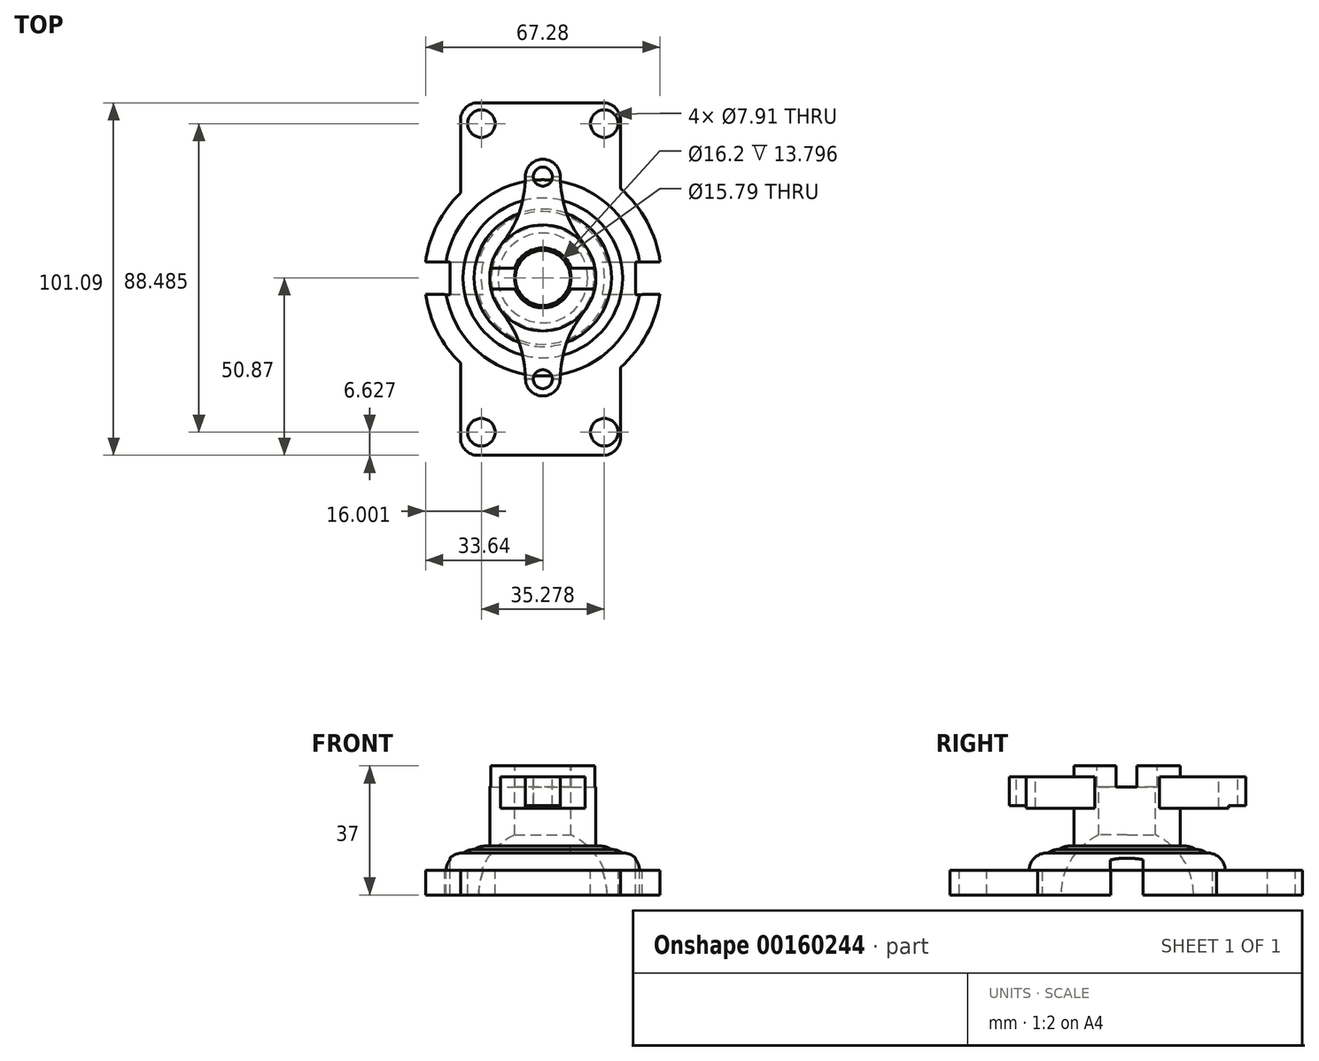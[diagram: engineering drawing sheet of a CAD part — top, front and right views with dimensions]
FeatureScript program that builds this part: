
annotation { "Feature Type Name" : "Feature", "Feature Type Description" : "" }
export const myFeature = defineFeature(function(context is Context, id is Id, definition is map)
    precondition{}
    {
        {
            var Q0;
            Q0=qCreatedBy(makeId("Top.planeOp"),FACE);
            var sketch = newSketch(context, id + "F0", { "sketchPlane" : qUnion([Q0])});
            skLineSegment(sketch, "E0.bottom", {"start": v(-23.62, 50.22) * mm, "end": v(22.27, 50.22) * mm});
            skLineSegment(sketch, "E0.top", {"start": v(-23.62, -50.87) * mm, "end": v(22.27, -50.87) * mm});
            skLineSegment(sketch, "E0.left", {"start": v(-23.62, 50.22) * mm, "end": v(-23.62, -50.87) * mm});
            skLineSegment(sketch, "E0.right", {"start": v(22.27, 50.22) * mm, "end": v(22.27, -50.87) * mm});
            skCircle(sketch, "E1", {"center": v(0, 0) * mm, "radius": 33.95 * mm});
            skSolve(sketch);
        }
        {
            var Q0;
            Q0 = qSketchRegion(id + "F0", true);
            extrude(context, id + "F1", {"entities" : qUnion([Q0]), "depth" : 7 * mm});
        }
        {
            var Q0;
            Q0=qCreatedBy(makeId("Top.planeOp"),FACE);
            var sketch = newSketch(context, id + "F2", { "sketchPlane" : qUnion([Q0])});
            skLineSegment(sketch, "E2.bottom", {"start": v(-35.85, -4.72) * mm, "end": v(38.25, -4.72) * mm});
            skLineSegment(sketch, "E2.top", {"start": v(-35.85, 4.53) * mm, "end": v(38.25, 4.53) * mm});
            skLineSegment(sketch, "E2.left", {"start": v(-35.85, -4.72) * mm, "end": v(-35.85, 4.53) * mm});
            skLineSegment(sketch, "E2.right", {"start": v(38.25, -4.72) * mm, "end": v(38.25, 4.53) * mm});
            skCircle(sketch, "E3", {"center": v(0, 0) * mm, "radius": 17.03 * mm});
            skSolve(sketch);
        }
        {
            var Q0;
            Q0 = qSketchRegion(id + "F2", true);
            extrude(context, id + "F3", {"entities" : qUnion([Q0]), "operationType" : NewBodyOperationType.REMOVE, "depth" : 7 * mm});
        }
        {
            var Q0;
            Q0=makeQuery(id+"F1.opExtrude","CAP_FACE",FACE,{"disambiguationData":[OSD([sQuery(id+"F0.wireOp",EDGE,"E0.bottom"),sQuery(id+"F0.wireOp",EDGE,"E0.top"),sQuery(id+"F0.wireOp",EDGE,"E0.left"),sQuery(id+"F0.wireOp",EDGE,"E0.right"),sQuery(id+"F0.wireOp",EDGE,"E1")])],"isStart":false});
            var sketch = newSketch(context, id + "F4", { "sketchPlane" : qUnion([Q0])});
            skCircle(sketch, "E4", {"center": v(0, 0) * mm, "radius": 28.12 * mm});
            skSolve(sketch);
        }
        {
            var Q0;
            Q0 = qSketchRegion(id + "F4", true);
            extrude(context, id + "F5", {"entities" : qUnion([Q0]), "operationType" : NewBodyOperationType.ADD, "depth" : 5 * mm});
        }
        {
            var Q0;
            Q0=makeQuery(id+"F5.opExtrude","CAP_EDGE",EDGE,{"disambiguationData":[OSD([sQuery(id+"F4.wireOp",EDGE,"E4")])],"isStart":false});
            fillet(context, id + "F6", {"entities" : qUnion([Q0]), "radius" : 5 * mm, "tangentPropagation" : true, "allowEdgeOverflow" : false});
        }
        {
            var Q0;
            Q0=makeQuery(id+"F5.opExtrude","CAP_FACE",FACE,{"disambiguationData":[OSD([sQuery(id+"F4.wireOp",EDGE,"E4")])],"isStart":false});
            var sketch = newSketch(context, id + "F7", { "sketchPlane" : qUnion([Q0])});
            skCircle(sketch, "E5", {"center": v(0, 0) * mm, "radius": 15.22 * mm});
            skSolve(sketch);
        }
        {
            var Q0;
            Q0=makeQuery(id+"F7.imprint","IMPRINT",FACE,{"disambiguationData":[TD([[makeQuery(id+"F7.imprint","IMPRINT",EDGE,{"derivedFrom":sQuery(id+"F7.wireOp",EDGE,"E5")}),1.0]])]});
            extrude(context, id + "F8", {"entities" : qUnion([Q0]), "operationType" : NewBodyOperationType.ADD, "depth" : 25 * mm});
        }
        {
            var Q0;
            Q0=makeQuery(id+"F8.opExtrude","CAP_FACE",FACE,{"disambiguationData":[OSD([sQuery(id+"F7.wireOp",EDGE,"E5")])],"isStart":false});
            var sketch = newSketch(context, id + "F9", { "sketchPlane" : qUnion([Q0])});
            skLineSegment(sketch, "E6.bottom", {"start": v(-18.99, 2.8) * mm, "end": v(19.76, 2.8) * mm});
            skLineSegment(sketch, "E6.top", {"start": v(-18.99, -3.18) * mm, "end": v(19.76, -3.18) * mm});
            skLineSegment(sketch, "E6.left", {"start": v(-18.99, 2.8) * mm, "end": v(-18.99, -3.18) * mm});
            skLineSegment(sketch, "E6.right", {"start": v(19.76, 2.8) * mm, "end": v(19.76, -3.18) * mm});
            skCircle(sketch, "E7", {"center": v(0, 0) * mm, "radius": 8.6 * mm});
            skSolve(sketch);
        }
        {
            var Q0;
            Q0 = qSketchRegion(id + "F9", true);
            extrude(context, id + "F10", {"entities" : qUnion([Q0]), "operationType" : NewBodyOperationType.REMOVE, "oppositeDirection" : true, "depth" : 6 * mm});
        }
        {
            var Q0;
            Q0=makeQuery(id+"F10.boolean.opBoolean","COPY",FACE,{"derivedFrom":makeQuery(id+"F10.opExtrude","CAP_FACE",FACE,{"disambiguationData":[OSD([sQuery(id+"F9.wireOp",EDGE,"E6.bottom"),sQuery(id+"F9.wireOp",EDGE,"E6.top"),sQuery(id+"F9.wireOp",EDGE,"E6.left"),sQuery(id+"F9.wireOp",EDGE,"E6.right"),sQuery(id+"F9.wireOp",EDGE,"E7")])],"isStart":false})});
            var sketch = newSketch(context, id + "F11", { "sketchPlane" : qUnion([Q0])});
            skCircle(sketch, "E8", {"center": v(0, 0) * mm, "radius": 8.1 * mm});
            skSolve(sketch);
        }
        {
            var Q0;
            Q0 = qSketchRegion(id + "F11", true);
            extrude(context, id + "F12", {"entities" : qUnion([Q0]), "operationType" : NewBodyOperationType.REMOVE, "oppositeDirection" : true, "depth" : 30 * mm});
        }
        {
            var Q0;
            {var subQ0=sQuery(id+"F0.wireOp",EDGE,"E1");var subQ1=sQuery(id+"F0.wireOp",EDGE,"E0.left");var subQ6=sQuery(id+"F0.wireOp",EDGE,"E0.right");var subQ7=sQuery(id+"F0.wireOp",EDGE,"E0.bottom");Q0=makeQuery(id+"F3.boolean.opBoolean","SPLIT",FACE,{"disambiguationData":[TD([makeQuery(id+"F1.opExtrude","SWEPT_FACE",FACE,{"disambiguationData":[OSD([subQ7])]})])],"derivedFrom":makeQuery(id+"F1.opExtrude","CAP_FACE",FACE,{"disambiguationData":[OSD([subQ7,sQuery(id+"F0.wireOp",EDGE,"E0.top"),subQ1,subQ6,subQ0])],"isStart":false})});}
            var sketch = newSketch(context, id + "F13", { "sketchPlane" : qUnion([Q0])});
            skCircle(sketch, "E9", {"center": v(-17.64, 44.24) * mm, "radius": 3.96 * mm});
            skCircle(sketch, "E10.MirrorC", {"center": v(17.64, 44.24) * mm, "radius": 3.96 * mm});
            skCircle(sketch, "E11.MirrorC", {"center": v(-17.64, -44.24) * mm, "radius": 3.96 * mm});
            skCircle(sketch, "E12.MirrorC", {"center": v(17.64, -44.24) * mm, "radius": 3.96 * mm});
            skSolve(sketch);
        }
        {
            var Q0;
            Q0=qCreatedBy(makeId("Right.planeOp"),FACE);
            var sketch = newSketch(context, id + "F14", { "sketchPlane" : qUnion([Q0])});
            skLineSegment(sketch, "E13.bottom", {"start": v(-13.4, 33.83) * mm, "end": v(-33.83, 33.83) * mm});
            skLineSegment(sketch, "E13.top", {"start": v(-13.4, 25.54) * mm, "end": v(-33.83, 25.54) * mm});
            skLineSegment(sketch, "E13.left", {"start": v(-13.4, 33.83) * mm, "end": v(-13.4, 25.54) * mm});
            skLineSegment(sketch, "E13.right", {"start": v(-33.83, 33.83) * mm, "end": v(-33.83, 25.54) * mm});
            skLineSegment(sketch, "E14.bottom", {"start": v(13.75, 33.83) * mm, "end": v(34.03, 33.83) * mm});
            skLineSegment(sketch, "E14.top", {"start": v(13.75, 25.54) * mm, "end": v(34.03, 25.54) * mm});
            skLineSegment(sketch, "E14.left", {"start": v(13.75, 33.83) * mm, "end": v(13.75, 25.54) * mm});
            skLineSegment(sketch, "E14.right", {"start": v(34.03, 33.83) * mm, "end": v(34.03, 25.54) * mm});
            skSolve(sketch);
        }
        {
            var Q0;
            Q0 = qSketchRegion(id + "F14", true);
            extrude(context, id + "F15", {"entities" : qUnion([Q0]), "operationType" : NewBodyOperationType.ADD, "endBound" : BoundingType.SYMMETRIC, "depth" : 10 * mm});
        }
        {
            var Q0;
            Q0=makeQuery(id+"F15.opExtrude","CAP_EDGE",EDGE,{"disambiguationData":[OSD([sQuery(id+"F14.wireOp",EDGE,"E14.right")])],"isStart":true});
            var Q1;
            Q1=makeQuery(id+"F15.opExtrude","CAP_EDGE",EDGE,{"disambiguationData":[OSD([sQuery(id+"F14.wireOp",EDGE,"E14.right")])],"isStart":false});
            var Q2;
            Q2=makeQuery(id+"F15.opExtrude","CAP_EDGE",EDGE,{"disambiguationData":[OSD([sQuery(id+"F14.wireOp",EDGE,"E13.right")])],"isStart":true});
            var Q3;
            Q3=makeQuery(id+"F15.opExtrude","CAP_EDGE",EDGE,{"disambiguationData":[OSD([sQuery(id+"F14.wireOp",EDGE,"E13.right")])],"isStart":false});
            fillet(context, id + "F16", {"entities" : qUnion([Q0, Q1, Q2, Q3]), "radius" : 5 * mm, "tangentPropagation" : true, "allowEdgeOverflow" : false});
        }
        {
            var Q0;
            Q0=makeQuery(id+"F15.opExtrude","SWEPT_FACE",FACE,{"disambiguationData":[OSD([sQuery(id+"F14.wireOp",EDGE,"E14.bottom")])]});
            var sketch = newSketch(context, id + "F17", { "sketchPlane" : qUnion([Q0])});
            skCircle(sketch, "E15", {"center": v(0, 29.03) * mm, "radius": 2.72 * mm});
            skCircle(sketch, "E16.MirrorC", {"center": v(0, -29.03) * mm, "radius": 2.72 * mm});
            skSolve(sketch);
        }
        {
            var Q0;
            Q0 = qSketchRegion(id + "F17", true);
            extrude(context, id + "F18", {"entities" : qUnion([Q0]), "operationType" : NewBodyOperationType.REMOVE, "oppositeDirection" : true, "depth" : 10 * mm});
        }
        {
            var Q0;
            Q0 = qSketchRegion(id + "F13", true);
            extrude(context, id + "F19", {"entities" : qUnion([Q0]), "operationType" : NewBodyOperationType.REMOVE, "oppositeDirection" : true, "depth" : 25 * mm});
        }
        {
            var Q0;
            Q0=qCreatedBy(makeId("Front.planeOp"),FACE);
            var sketch = newSketch(context, id + "F20", { "sketchPlane" : qUnion([Q0])});
            skCircle(sketch, "E17", {"center": v(0, 0) * mm, "radius": 19.02 * mm});
            skLineSegment(sketch, "E18", {"start": v(0, -19.02) * mm, "end": v(0, 19.02) * mm});
            skSolve(sketch);
        }
        {
            var Q0;
            {var subQ0=sQuery(id+"F20.wireOp",EDGE,"E18");Q0=makeQuery(id+"F20.imprint","IMPRINT",FACE,{"disambiguationData":[TD([[makeQuery(id+"F20.imprint","IMPRINT",EDGE,{"derivedFrom":subQ0}),-1.0]])]});}
            var Q1;
            Q1=sQuery(id+"F20.wireOp",EDGE,"E18");
            revolve(context, id + "F21", {"operationType" : NewBodyOperationType.REMOVE, "entities" : qUnion([Q0]), "axis" : qUnion([Q1]), "revolveType" : RevolveType.FULL, "oppositeDirection" : true});
        }
        {
            var Q0;
            Q0=makeQuery(id+"F1.opExtrude","SWEPT_EDGE",EDGE,{"disambiguationData":[OSD([sQuery(id+"F0.wireOp",EDGE,"E0.top"),sQuery(id+"F0.wireOp",EDGE,"E0.right")])]});
            var Q1;
            Q1=makeQuery(id+"F1.opExtrude","SWEPT_EDGE",EDGE,{"disambiguationData":[OSD([sQuery(id+"F0.wireOp",EDGE,"E0.top"),sQuery(id+"F0.wireOp",EDGE,"E0.left")])]});
            var Q2;
            Q2=makeQuery(id+"F1.opExtrude","SWEPT_EDGE",EDGE,{"disambiguationData":[OSD([sQuery(id+"F0.wireOp",EDGE,"E0.bottom"),sQuery(id+"F0.wireOp",EDGE,"E0.right")])]});
            var Q3;
            Q3=makeQuery(id+"F1.opExtrude","SWEPT_EDGE",EDGE,{"disambiguationData":[OSD([sQuery(id+"F0.wireOp",EDGE,"E0.bottom"),sQuery(id+"F0.wireOp",EDGE,"E0.left")])]});
            fillet(context, id + "F22", {"entities" : qUnion([Q0, Q1, Q2, Q3]), "radius" : 5 * mm, "tangentPropagation" : true, "allowEdgeOverflow" : false});
        }
        {
            var Q0;
            Q0=makeQuery(id+"F5.opExtrude","CAP_FACE",FACE,{"disambiguationData":[OSD([sQuery(id+"F4.wireOp",EDGE,"E4")])],"isStart":false});
            var sketch = newSketch(context, id + "F23", { "sketchPlane" : qUnion([Q0])});
            skCircle(sketch, "E19", {"center": v(0, 0) * mm, "radius": 22.86 * mm});
            skSolve(sketch);
        }
        {
            var Q0;
            Q0 = qSketchRegion(id + "F23", true);
            extrude(context, id + "F24", {"entities" : qUnion([Q0]), "operationType" : NewBodyOperationType.ADD, "depth" : 1 * mm});
        }
        {
            var Q0;
            Q0=makeQuery(id+"F24.opExtrude","CAP_EDGE",EDGE,{"disambiguationData":[OSD([sQuery(id+"F23.wireOp",EDGE,"E19")])],"isStart":false});
            fillet(context, id + "F25", {"entities" : qUnion([Q0]), "radius" : 5 * mm, "tangentPropagation" : true, "allowEdgeOverflow" : false});
        }
        {
            var Q0;
            {var subQ0=sQuery(id+"F23.wireOp",EDGE,"E19");Q0=makeQuery(id+"F24.boolean.opBoolean","SPLIT",FACE,{"disambiguationData":[TD([makeQuery(id+"F8.opExtrude","SWEPT_FACE",FACE,{"disambiguationData":[OSD([sQuery(id+"F7.wireOp",EDGE,"E5")])]})])],"derivedFrom":makeQuery(id+"F24.opExtrude","CAP_FACE",FACE,{"disambiguationData":[OSD([subQ0])],"isStart":false})});}
            var sketch = newSketch(context, id + "F26", { "sketchPlane" : qUnion([Q0])});
            skCircle(sketch, "E20", {"center": v(0, 0) * mm, "radius": 19.69 * mm});
            skSolve(sketch);
        }
        {
            var Q0;
            Q0 = qSketchRegion(id + "F26", true);
            extrude(context, id + "F27", {"entities" : qUnion([Q0]), "operationType" : NewBodyOperationType.ADD, "depth" : 1 * mm});
        }
        {
            var Q0;
            Q0=makeQuery(id+"F27.opExtrude","CAP_EDGE",EDGE,{"disambiguationData":[OSD([sQuery(id+"F26.wireOp",EDGE,"E20")])],"isStart":false});
            fillet(context, id + "F28", {"entities" : qUnion([Q0]), "radius" : 5 * mm, "tangentPropagation" : true, "allowEdgeOverflow" : false});
        }
        {
            var Q0;
            Q0=makeQuery(id+"F27.boolean.opBoolean","SPLIT",FACE,{"disambiguationData":[TD([makeQuery(id+"F21.boolean.opBoolean","COPY",FACE,{"derivedFrom":makeQuery(id+"F21.opRevolve","SWEPT_FACE",FACE,{"disambiguationData":[OSD([sQuery(id+"F20.wireOp",EDGE,"E17")])]})})])],"derivedFrom":makeQuery(id+"F27.opExtrude","CAP_FACE",FACE,{"disambiguationData":[OSD([sQuery(id+"F26.wireOp",EDGE,"E20")])],"isStart":false})});
            var sketch = newSketch(context, id + "F29", { "sketchPlane" : qUnion([Q0])});
            skCircle(sketch, "E21", {"center": v(0, 0) * mm, "radius": 7.9 * mm});
            skSolve(sketch);
        }
        {
            var Q0;
            Q0 = qSketchRegion(id + "F29", true);
            extrude(context, id + "F30", {"entities" : qUnion([Q0]), "operationType" : NewBodyOperationType.REMOVE, "oppositeDirection" : true, "depth" : 25 * mm});
        }
        {
            var Q0;
            Q0=makeQuery(id+"F15.opExtrude","SWEPT_FACE",FACE,{"disambiguationData":[OSD([sQuery(id+"F14.wireOp",EDGE,"E14.bottom")])]});
            var sketch = newSketch(context, id + "F31", { "sketchPlane" : qUnion([Q0])});
            skArc(sketch, "E22", {"start": v(-12.18, 9.3) * mm, "mid": v(-6.85, 18.53) * mm, "end": v(-5, 29.03) * mm});
            skArc(sketch, "E23.MirrorCS", {"start": v(12.18, 9.3) * mm, "mid": v(6.85, 18.53) * mm, "end": v(5, 29.03) * mm});
            skLineSegment(sketch, "E24", {"start": v(-5, 29.03) * mm, "end": v(5, 29.03) * mm});
            skLineSegment(sketch, "E25", {"start": v(-12.18, 9.3) * mm, "end": v(12.18, 9.3) * mm});
            skArc(sketch, "E26.MirrorCS", {"start": v(-12.18, -9.3) * mm, "mid": v(-6.85, -18.53) * mm, "end": v(-5, -29.03) * mm});
            skArc(sketch, "E27.MirrorCS", {"start": v(12.18, -9.3) * mm, "mid": v(6.85, -18.53) * mm, "end": v(5, -29.03) * mm});
            skLineSegment(sketch, "E28.MirrorCS", {"start": v(-12.18, -9.3) * mm, "end": v(12.18, -9.3) * mm});
            skLineSegment(sketch, "E29.MirrorCS", {"start": v(-5, -29.03) * mm, "end": v(5, -29.03) * mm});
            skSolve(sketch);
        }
        {
            var Q0;
            Q0 = qSketchRegion(id + "F31", true);
            extrude(context, id + "F32", {"entities" : qUnion([Q0]), "operationType" : NewBodyOperationType.ADD, "oppositeDirection" : true, "depth" : 9 * mm});
        }
        {
            var Q0;
            Q0=makeQuery(id+"F32.boolean.opBoolean","MERGE",FACE,{"derivedFrom":[makeQuery(id+"F15.opExtrude","SWEPT_FACE",FACE,{"disambiguationData":[OSD([sQuery(id+"F14.wireOp",EDGE,"E14.bottom")])]}),makeQuery(id+"F32.opExtrude","CAP_FACE",FACE,{"disambiguationData":[OSD([sQuery(id+"F31.wireOp",EDGE,"E22"),sQuery(id+"F31.wireOp",EDGE,"E23.MirrorCS"),sQuery(id+"F31.wireOp",EDGE,"E24"),sQuery(id+"F31.wireOp",EDGE,"E25")])],"isStart":true})]});
            var sketch = newSketch(context, id + "F33", { "sketchPlane" : qUnion([Q0])});
            skCircle(sketch, "E30", {"center": v(0, 29.03) * mm, "radius": 2.71 * mm});
            skCircle(sketch, "E31.MirrorC", {"center": v(0, -29.03) * mm, "radius": 2.71 * mm});
            skSolve(sketch);
        }
        {
            var Q0;
            Q0 = qSketchRegion(id + "F33", true);
            extrude(context, id + "F34", {"entities" : qUnion([Q0]), "operationType" : NewBodyOperationType.REMOVE, "oppositeDirection" : true, "depth" : 10 * mm});
        }
        {
            var Q0;
            {var subQ0=sQuery(id+"F0.wireOp",EDGE,"E1");var subQ1=sQuery(id+"F0.wireOp",EDGE,"E0.left");var subQ6=sQuery(id+"F0.wireOp",EDGE,"E0.right");var subQ7=sQuery(id+"F0.wireOp",EDGE,"E0.bottom");Q0=makeQuery(id+"F3.boolean.opBoolean","SPLIT",FACE,{"disambiguationData":[TD([makeQuery(id+"F1.opExtrude","SWEPT_FACE",FACE,{"disambiguationData":[OSD([subQ7])]})])],"derivedFrom":makeQuery(id+"F1.opExtrude","CAP_FACE",FACE,{"disambiguationData":[OSD([subQ7,sQuery(id+"F0.wireOp",EDGE,"E0.top"),subQ1,subQ6,subQ0])],"isStart":false})});}
            var sketch = newSketch(context, id + "F35", { "sketchPlane" : qUnion([Q0])});
            skLineSegment(sketch, "E32.bottom", {"start": v(-27.76, 4.53) * mm, "end": v(-26.67, 4.53) * mm});
            skLineSegment(sketch, "E32.top", {"start": v(-27.76, -4.8) * mm, "end": v(-26.67, -4.8) * mm});
            skLineSegment(sketch, "E32.left", {"start": v(-27.76, 4.53) * mm, "end": v(-27.76, -4.8) * mm});
            skLineSegment(sketch, "E32.right", {"start": v(-26.67, 4.53) * mm, "end": v(-26.67, -4.8) * mm});
            skLineSegment(sketch, "E33.bottom", {"start": v(27.76, 4.53) * mm, "end": v(26.66, 4.53) * mm});
            skLineSegment(sketch, "E33.top", {"start": v(27.76, -4.83) * mm, "end": v(26.66, -4.83) * mm});
            skLineSegment(sketch, "E33.left", {"start": v(27.76, 4.53) * mm, "end": v(27.76, -4.83) * mm});
            skLineSegment(sketch, "E33.right", {"start": v(26.66, 4.53) * mm, "end": v(26.66, -4.83) * mm});
            skLineSegment(sketch, "E34.bottom", {"start": v(27.76, 4.53) * mm, "end": v(28.44, 4.53) * mm});
            skLineSegment(sketch, "E34.top", {"start": v(27.76, -4.82) * mm, "end": v(28.44, -4.82) * mm});
            skLineSegment(sketch, "E34.left", {"start": v(27.76, 4.53) * mm, "end": v(27.76, -4.82) * mm});
            skLineSegment(sketch, "E34.right", {"start": v(28.44, 4.53) * mm, "end": v(28.44, -4.82) * mm});
            skLineSegment(sketch, "E35.bottom", {"start": v(-27.76, 4.53) * mm, "end": v(-28.18, 4.53) * mm});
            skLineSegment(sketch, "E35.top", {"start": v(-27.76, -4.86) * mm, "end": v(-28.18, -4.86) * mm});
            skLineSegment(sketch, "E35.left", {"start": v(-27.76, 4.53) * mm, "end": v(-27.76, -4.86) * mm});
            skLineSegment(sketch, "E35.right", {"start": v(-28.18, 4.53) * mm, "end": v(-28.18, -4.86) * mm});
            skSolve(sketch);
        }
        {
            var Q0;
            Q0 = qSketchRegion(id + "F35", true);
            extrude(context, id + "F36", {"entities" : qUnion([Q0]), "operationType" : NewBodyOperationType.REMOVE, "endBound" : BoundingType.SYMMETRIC, "oppositeDirection" : true, "depth" : 25 * mm});
        }
        {
            var Q0;
            Q0 = qSketchRegion(id + "F35", true);
            extrude(context, id + "F37", {"entities" : qUnion([Q0]), "operationType" : NewBodyOperationType.REMOVE, "endBound" : BoundingType.SYMMETRIC, "oppositeDirection" : true, "depth" : 3 * mm});
        }
    });
